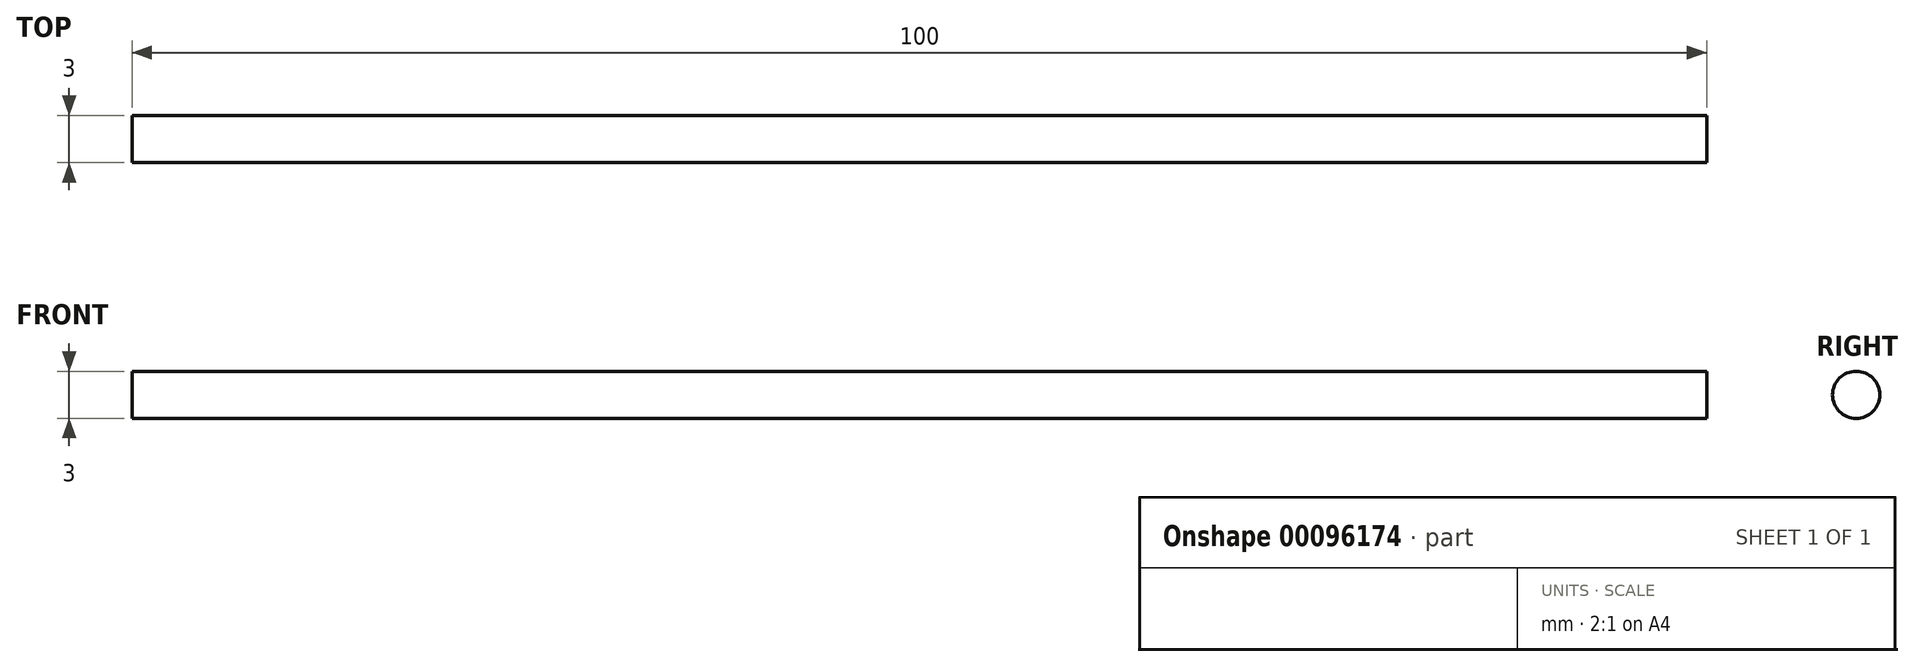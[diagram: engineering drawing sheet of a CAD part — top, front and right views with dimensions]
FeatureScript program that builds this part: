
annotation { "Feature Type Name" : "Feature", "Feature Type Description" : "" }
export const myFeature = defineFeature(function(context is Context, id is Id, definition is map)
    precondition{}
    {
        {
            var Q0;
            Q0=qCreatedBy(makeId("Right.planeOp"),FACE);
            var sketch = newSketch(context, id + "F0", { "sketchPlane" : qUnion([Q0])});
            skCircle(sketch, "E0", {"center": v(0, 0) * mm, "radius": 1.5 * mm});
            skSolve(sketch);
        }
        {
            var Q0;
            Q0=qSketchRegion(id+"F0",true);
            extrude(context, id + "F1", {"entities" : qUnion([Q0]), "depth" : 50 * mm, "hasSecondDirection" : true, "secondDirectionOppositeDirection" : true, "secondDirectionDepth" : 50 * mm});
        }
    });
